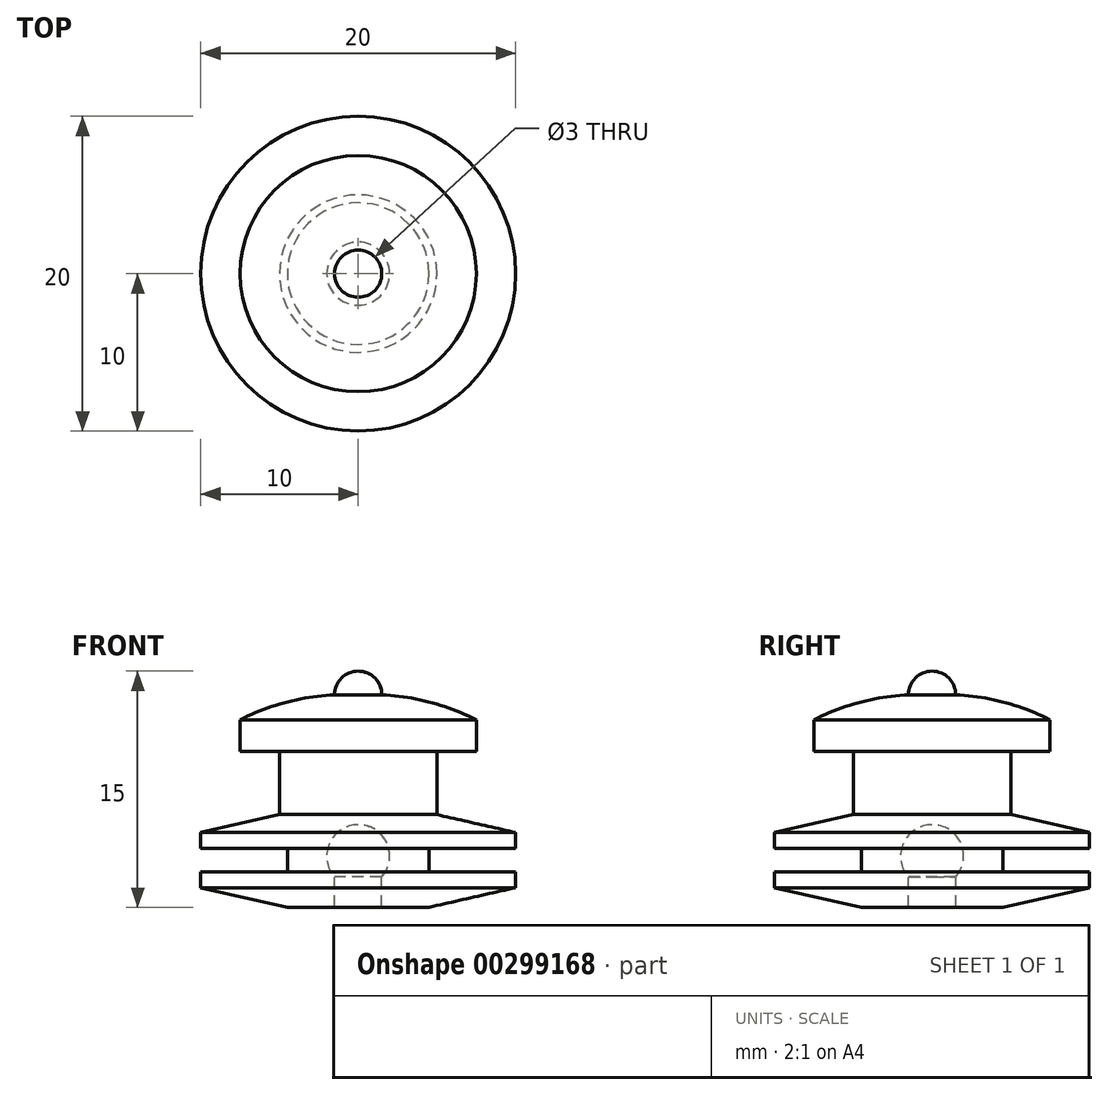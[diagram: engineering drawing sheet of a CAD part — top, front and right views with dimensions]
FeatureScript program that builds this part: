
annotation { "Feature Type Name" : "Feature", "Feature Type Description" : "" }
export const myFeature = defineFeature(function(context is Context, id is Id, definition is map)
    precondition{}
    {
        {
            var Q0;
            Q0=qCreatedBy(makeId("Front.planeOp"),FACE);
            var sketch = newSketch(context, id + "F0", { "sketchPlane" : qUnion([Q0])});
            skArc(sketch, "E0", {"start": v(1.5, 13.5) * mm, "mid": v(1.06, 14.56) * mm, "end": v(0, 15) * mm});
            skLineSegment(sketch, "E1", {"start": v(1.5, 0) * mm, "end": v(4.5, 0) * mm});
            skLineSegment(sketch, "E2", {"start": v(4.5, 0) * mm, "end": v(4.5, 3.75) * mm});
            skArc(sketch, "E3", {"start": v(1.5, 1.93) * mm, "mid": v(1.82, 4.07) * mm, "end": v(0, 5.25) * mm});
            skLineSegment(sketch, "E4", {"start": v(1.5, 1.93) * mm, "end": v(1.5, 0) * mm});
            skLineSegment(sketch, "E5", {"start": v(4.5, 3.75) * mm, "end": v(10, 3.75) * mm});
            skLineSegment(sketch, "E6", {"start": v(10, 3.75) * mm, "end": v(10, 4.75) * mm});
            skPoint(sketch, "E7.orphan", {"position": v(1.94, 3.75) * mm});
            skLineSegment(sketch, "E8", {"start": v(5, 5.89) * mm, "end": v(5, 9.89) * mm});
            skLineSegment(sketch, "E9", {"start": v(5, 9.89) * mm, "end": v(7.5, 9.89) * mm});
            skLineSegment(sketch, "E10", {"start": v(7.5, 9.89) * mm, "end": v(7.5, 11.91) * mm});
            skLineSegment(sketch, "E11", {"start": v(0, 13.5) * mm, "end": v(0, 15) * mm});
            skArc(sketch, "E12.trimOffspring", {"start": v(7.5, 11.91) * mm, "mid": v(4.58, 13.02) * mm, "end": v(1.5, 13.5) * mm});
            skPoint(sketch, "E13.center.orphan", {"position": v(0, -1.5) * mm});
            skLineSegment(sketch, "E14", {"start": v(0, 13.5) * mm, "end": v(0, 5.25) * mm});
            skLineSegment(sketch, "E15", {"start": v(4.5, 2.25) * mm, "end": v(10, 2.25) * mm});
            skLineSegment(sketch, "E16", {"start": v(4.5, 3) * mm, "end": v(10, 3) * mm, "construction": true});
            skLineSegment(sketch, "E17", {"start": v(10, 2.25) * mm, "end": v(10, 1.25) * mm});
            skPoint(sketch, "E18.orphan", {"position": v(5, 0.11) * mm});
            skLineSegment(sketch, "E19", {"start": v(5, 5.89) * mm, "end": v(10, 4.75) * mm});
            skLineSegment(sketch, "E20", {"start": v(4.5, 0) * mm, "end": v(10, 1.25) * mm});
            skSolve(sketch);
        }
        {
            var Q0;
            Q0 = qSketchRegion(id + "F0", true);
            var Q1;
            Q1=sQuery(id+"F0.wireOp",EDGE,"E14");
            revolve(context, id + "F1", {"entities" : qUnion([Q0]), "axis" : qUnion([Q1]), "revolveType" : RevolveType.FULL});
        }
    });
